# Revit family: Haworth_Aloha_Easy_Chair_Task_Executive_AP_PRELIMINARY
name_source: partatom
category: Furniture
units: mm (PartAtom-declared; Revit-internal decimal feet)

## family parameters
Always vertical = Yes
Cut with Voids When Loaded = No
OmniClass Number = 23.40.70.14.64.11
OmniClass Title = Office Furniture
Room Calculation Point = No
Shared = No
Work Plane-Based = No

## types (3) — shared parameters
Arm Finish = Haworth _ Paint _ Smoke
Assembly Code = E2020200
Caster Finish = Haworth _ Polymer _ Undecided
Depth = 737 mm
Description = Haworth - Aloha Easy - Task Chair - Executive
Headrest Backer = Haworth _ Polymer _ Slate
Manufacturer = Haworth
Model = SE65EEMX
Revision Number = 1
Size = Verify Final.Dim w/Haworth
URL = https://www.haworth.com
URL - Product = https://www.haworth.com
Warranty = http://www.haworth.com
Width = 737 mm

## per-type parameters (varying)
| type | 4D Arms | With Arms | Without Arms |
| 4D Arms | Yes | Yes | No |
| No Arm | No | No | Yes |
| Height Adjustable Arms | No | Yes | No |

type visibility flags (boolean, named after types; folded from table):
- 4D Arms: Yes: (none)
- No Arm: Yes: (none)
- Height Adjustable Arms: Yes: Height Adjustable Arms

## geometry (parser evidence)
native form markers: Blend x2, Sweep x11
no freeform markers — native parametric forms only
